FCSTD DOCUMENT  (FreeCAD 0.16R)
Label: chainguard30t
License: All rights reserved
LicenseURL: http://en.wikipedia.org/wiki/All_rights_reserved
objects: Sketcher::SketchObject×12, PartDesign::Pocket×6, PartDesign::Pad×5, Mesh::Feature×4, PartDesign::Fillet×1
note: 35 computed .brp shape members not serialized (recipe doc carries the construction recipe); baked Part::Feature solids carry a one-line shape summary decoded from their .brp

FEATURE [Sketcher::SketchObject] Sketch001
  sketch-geometry (7):
    g0: LineSegment StartX=50 StartY=74 StartZ=0 EndX=0 EndY=74 EndZ=0
    g1: LineSegment StartX=50 StartY=-74 StartZ=0 EndX=0 EndY=-74 EndZ=0
    g2: ArcOfCircle CenterX=0.00010789 CenterY=0 CenterZ=0 NormalX=0 NormalY=0 NormalZ=1 Radius=74 StartAngle=1.5708 EndAngle=4.71239
    g3: Circle CenterX=0 CenterY=0 CenterZ=0 NormalX=0 NormalY=0 NormalZ=1 Radius=45
    g4: LineSegment StartX=73 StartY=51 StartZ=0 EndX=73 EndY=-51 EndZ=0
    g5: ArcOfCircle CenterX=50 CenterY=51 CenterZ=0 NormalX=0 NormalY=0 NormalZ=1 Radius=23 StartAngle=0 EndAngle=1.5708
    g6: ArcOfCircle CenterX=50 CenterY=-51 CenterZ=0 NormalX=0 NormalY=0 NormalZ=1 Radius=23 StartAngle=4.71239 EndAngle=6.28319
  constraints (22):
    c: Horizontal(g0)
    c: Horizontal(g1)
    c: Coincident(g2,g1)
    c: Coincident(g0,g2)
    c: DistanceX(g1,g0) = 0
    c: Equal(g0,g1)
    c: DistanceY(g1,g0) = 148
    c: Symmetric(g1,g0,g-1)
    c: Radius(g3) = 45
    c: Coincident(g3,g-1)
    c: DistanceX(g0,g0) = 50
    c: Vertical(g4)
    c: DistanceX(g-1,g4) = 73
    c: Symmetric(g4,g4,g-1)
    c: DistanceY(g4,g4) = 102
    c: Coincident(g5,g4)
    c: Coincident(g5,g0)
    c: Coincident(g6,g4)
    c: Coincident(g6,g1)
    c: Equal(g5,g6)
    c: Radius(g5) = 23
    c: Radius(g2) = 74
FEATURE [PartDesign::Pad] Pad  label="Faceplate"
  Length = 1.12
  Length2 = 100
  Reversed = true
  Sketch = -> Sketch001
  Type = 0
FEATURE [Sketcher::SketchObject] Sketch002
  sketch-geometry (8):
    g0: LineSegment StartX=50 StartY=74 StartZ=0 EndX=0 EndY=74 EndZ=0
    g1: LineSegment StartX=50 StartY=-74 StartZ=0 EndX=0 EndY=-74 EndZ=0
    g2: ArcOfCircle CenterX=0.000113412 CenterY=0 CenterZ=0 NormalX=0 NormalY=0 NormalZ=1 Radius=74 StartAngle=1.5708 EndAngle=4.71239
    g3: LineSegment StartX=0 StartY=72 StartZ=0 EndX=50 EndY=72 EndZ=0
    g4: LineSegment StartX=0 StartY=-72 StartZ=0 EndX=50 EndY=-72 EndZ=0
    g5: LineSegment StartX=50 StartY=74 StartZ=0 EndX=50 EndY=72 EndZ=0
    g6: LineSegment StartX=50 StartY=-72 StartZ=0 EndX=50 EndY=-74 EndZ=0
    g7: ArcOfCircle CenterX=7.04967e-05 CenterY=0 CenterZ=0 NormalX=0 NormalY=0 NormalZ=1 Radius=72 StartAngle=1.5708 EndAngle=4.71239
  constraints (25):
    c: Horizontal(g0)
    c: Horizontal(g1)
    c: Coincident(g2,g1)
    c: Coincident(g0,g2)
    c: DistanceX(g1,g0) = 0
    c: Equal(g0,g1)
    c: DistanceY(g1,g0) = 148
    c: Symmetric(g1,g0,g-1)
    c: Parallel(g0,g3)
    c: DistanceY(g3,g0) = 2
    c: DistanceY(g1,g4) = 2
    c: Parallel(g4,g1)
    c: DistanceX(g0,g3) = 0
    c: DistanceX(g4) = 0
    c: DistanceX(g0) = 50
    c: Equal(g3,g0)
    c: Equal(g4,g0)
    c: Coincident(g4,g6)
    c: Coincident(g6,g1)
    c: Coincident(g5,g3)
    c: Coincident(g5,g0)
    c: Coincident(g7,g3)
    c: Coincident(g7,g4)
    c: Radius(g7) = 72
    c: Radius(g2) = 74
FEATURE [PartDesign::Pad] Pad001  label="Connector"
  Length = 10
  Length2 = 100
  Sketch = -> Sketch002
  Type = 0
FEATURE [Sketcher::SketchObject] Sketch011
  Placement = pos=(0,74,0) rot=(0,0.707107,0.707107;3.14159rad)
  Support = -> Pad001 [Face1]
  sketch-geometry (4):
    g0: LineSegment StartX=-42 StartY=11 StartZ=0 EndX=-54.6477 EndY=14.0061 EndZ=0
    g1: LineSegment StartX=-54.6477 StartY=14.0061 StartZ=0 EndX=-50.9272 EndY=1.54985 EndZ=0
    g2: LineSegment StartX=-50.9272 StartY=1.54985 StartZ=0 EndX=-42 EndY=11 EndZ=0
    g3: Circle [constr] CenterX=-49.1916 CenterY=8.85198 CenterZ=0 NormalX=0 NormalY=0 NormalZ=1 Radius=7.50555
  constraints (14):
    c: Coincident(g0,g1)
    c: Coincident(g1,g2)
    c: Coincident(g2,g0)
    c: Equal(g0,g1)
    c: Equal(g0,g2)
    c: PointOnObject(g0,g3)
    c: PointOnObject(g1,g3)
    c: PointOnObject(g2,g3)
    c: DistanceY(g-1,g0) = 11
    c: DistanceX(g0,g-1) = 42
    c: Equal(g2,g0)
    c: Equal(g0,g1)
    c: Distance(g2) = 13
    c: Angle(g0) = 2.90824
FEATURE [PartDesign::Pocket] Pocket005  label="Bevel_connector"
  Length = 5
  Sketch = -> Sketch011
  Type = 1
FEATURE [Sketcher::SketchObject] Sketch017
  sketch-geometry (5):
    g0: LineSegment [constr] StartX=-4 StartY=2 StartZ=0 EndX=-27.8283 EndY=-75.9388 EndZ=0
    g1: LineSegment StartX=-43.448 StartY=-67.1734 StartZ=0 EndX=-9.97737 EndY=-77.4064 EndZ=0
    g2: LineSegment StartX=-9.97737 StartY=-77.4064 StartZ=0 EndX=-8.22314 EndY=-71.6686 EndZ=0
    g3: LineSegment StartX=-8.22314 StartY=-71.6686 StartZ=0 EndX=-41.6938 EndY=-61.4356 EndZ=0
    g4: LineSegment StartX=-41.6938 StartY=-61.4356 StartZ=0 EndX=-43.448 EndY=-67.1734 EndZ=0
  constraints (15):
    c: DistanceY(g-1,g0) = 2
    c: DistanceX(g-1,g0) = -4
    c: Angle(g0) = -1.8675
    c: Coincident(g1,g2)
    c: Coincident(g2,g3)
    c: Coincident(g3,g4)
    c: Coincident(g1,g4)
    c: Parallel(g2,g4)
    c: Parallel(g1,g3)
    c: Perpendicular(g2,g1)
    c: Distance(g4) = 6
    c: Distance(g1) = 35
    c: Symmetric(g3,g2,g0)
    c: Distance(g-1,g1) = 80
    c: Distance(g0) = 81.5
FEATURE [Sketcher::SketchObject] Sketch020
  sketch-geometry (4):
    g0: LineSegment StartX=67 StartY=25 StartZ=0 EndX=73 EndY=25 EndZ=0
    g1: LineSegment StartX=73 StartY=25 StartZ=0 EndX=73 EndY=-35 EndZ=0
    g2: LineSegment StartX=73 StartY=-35 StartZ=0 EndX=67 EndY=-35 EndZ=0
    g3: LineSegment StartX=67 StartY=-35 StartZ=0 EndX=67 EndY=25 EndZ=0
  constraints (12):
    c: Coincident(g0,g1)
    c: Coincident(g1,g2)
    c: Coincident(g2,g3)
    c: Coincident(g3,g0)
    c: Horizontal(g0)
    c: Horizontal(g2)
    c: Vertical(g1)
    c: Vertical(g3)
    c: DistanceX(g-1,g0) = 73
    c: DistanceX(g0,g0) = 6
    c: DistanceY(g-1,g0) = 25
    c: DistanceY(g1,g1) = 60
FEATURE [PartDesign::Pad] Pad004  label="SyncBoss"
  Length = 31
  Length2 = 100
  Sketch = -> Sketch020
  Type = 0
FEATURE [Sketcher::SketchObject] Sketch021
  ExternalGeometry = -> [Pad004]
  Placement = pos=(73,0,0) rot=(0.57735,0.57735,0.57735;2.0944rad)
  Support = -> Pad004 [Face2]
  sketch-geometry (1):
    g0: Circle CenterX=-5 CenterY=31 CenterZ=0 NormalX=0 NormalY=0 NormalZ=1 Radius=11.2
  constraints (2):
    c: Symmetric(g-4,g-3,g0)
    c: Radius(g0) = 11.2
FEATURE [PartDesign::Pocket] Pocket  label="SyncHole"
  Length = 5
  Sketch = -> Sketch021
  Type = 1
FEATURE [PartDesign::Pad] Pad005  label="STBoss"
  Length = 31
  Length2 = 1
  Sketch = -> Sketch017
  Type = 4
FEATURE [Sketcher::SketchObject] Sketch022
  ExternalGeometry = -> [Pad005]
  Placement = pos=(-22.4954,-73.5793,0) rot=(0.978386,-0.146221,-0.146221;1.59265rad)
  Support = -> Pad005 [Face1]
  sketch-geometry (1):
    g0: Circle CenterX=-4.40996 CenterY=31 CenterZ=0 NormalX=0 NormalY=0 NormalZ=1 Radius=11.2
  constraints (2):
    c: Symmetric(g-4,g-3,g0)
    c: Radius(g0) = 11.2
FEATURE [PartDesign::Pocket] Pocket006  label="SThole"
  Length = 5
  Sketch = -> Sketch022
  Type = 1
FEATURE [Sketcher::SketchObject] Sketch024
  sketch-geometry (6):
    g0: ArcOfCircle CenterX=0 CenterY=0 CenterZ=0 NormalX=0 NormalY=0 NormalZ=1 Radius=48 StartAngle=1.34179 EndAngle=4.9414
    g1: Circle CenterX=0 CenterY=0 CenterZ=0 NormalX=0 NormalY=0 NormalZ=1 Radius=45
    g2: LineSegment StartX=10.8966 StartY=46.7468 StartZ=0 EndX=65 EndY=35.4994 EndZ=0
    g3: LineSegment StartX=65 StartY=35.5006 StartZ=0 EndX=65 EndY=-35.4994 EndZ=0
    g4: LineSegment StartX=65 StartY=-35.4994 StartZ=0 EndX=10.8966 EndY=-46.7468 EndZ=0
    g5: LineSegment StartX=65 StartY=35.5 StartZ=0 EndX=65 EndY=-35.5 EndZ=0
  constraints (14):
    c: Coincident(g0,g-1)
    c: Radius(g0) = 48
    c: Coincident(g1,g-1)
    c: Radius(g1) = 45
    c: Coincident(g3,g4)
    c: Coincident(g0,g2)
    c: Distance(g3) = 71
    c: DistanceX(g-1,g2) = 65
    c: Equal(g4,g2)
    c: Vertical(g3)
    c: Symmetric(g2,g3,g-1)
    c: Distance(g2) = 55.2601
    c: DistanceY(g-1,g0) = 46.7468
    c: DistanceX(g0) = 10.8966
FEATURE [Sketcher::SketchObject] Sketch028
  ExternalGeometry = -> [Pocket]
  Placement = pos=(0,0,31) rot=(0,0,1;0rad)
  Support = -> Pocket [Face5]
  sketch-geometry (2):
    g0: Circle CenterX=70 CenterY=9 CenterZ=0 NormalX=0 NormalY=0 NormalZ=1 Radius=0.8
    g1: Circle CenterX=70 CenterY=-19 CenterZ=0 NormalX=0 NormalY=0 NormalZ=1 Radius=0.8
  constraints (6):
    c: DistanceY(g-4,g0) = 2.8
    c: DistanceX(g0,g-4) = 3
    c: DistanceX(g1,g-6) = 3
    c: DistanceY(g1,g-5) = 2.8
    c: Equal(g1,g0)
    c: Radius(g1) = 0.8
FEATURE [PartDesign::Pocket] Pocket010  label="SyncScrewHoles"
  Length = 15
  Sketch = -> Sketch028
  Type = 0
FEATURE [Sketcher::SketchObject] Sketch029
  ExternalGeometry = -> [Pocket010]
  Placement = pos=(73,0,0) rot=(0.57735,0.57735,0.57735;2.0944rad)
  Support = -> Pocket010 [Face3]
  sketch-geometry (6):
    g0: LineSegment StartX=25 StartY=3 StartZ=0 EndX=12.5 EndY=32 EndZ=0
    g1: LineSegment StartX=12.5 StartY=32 StartZ=0 EndX=-22.5 EndY=32 EndZ=0
    g2: LineSegment StartX=-22.5 StartY=32 StartZ=0 EndX=-35 EndY=3 EndZ=0
    g3: LineSegment StartX=-35 StartY=3 StartZ=0 EndX=-38.2949 EndY=52.1665 EndZ=0
    g4: LineSegment StartX=-38.2949 StartY=52.1665 StartZ=0 EndX=33.0613 EndY=52.1665 EndZ=0
    g5: LineSegment StartX=33.0613 StartY=52.1665 StartZ=0 EndX=25 EndY=3 EndZ=0
  constraints (18):
    c: Coincident(g0,g1)
    c: Horizontal(g1)
    c: Coincident(g1,g2)
    c: Coincident(g2,g3)
    c: Coincident(g3,g4)
    c: Horizontal(g4)
    c: Coincident(g4,g5)
    c: Coincident(g0,g5)
    c: DistanceX(g-4,g0) = 6.3
    c: DistanceX(g1,g-4) = 6.3
    c: DistanceX(g-3,g0) = 0
    c: DistanceX(g2,g-6) = 0
    c: DistanceX(g4,g4) = 71.3562
    c: Distance(g3) = 49.2768
    c: Distance(g5) = 49.823
    c: DistanceY(g-4,g1) = 1
    c: DistanceY(g-6,g2) = 3
    c: DistanceY(g-3,g0) = 3
FEATURE [PartDesign::Pocket] Pocket011  label="SyncBigBevel"
  Length = 5
  Sketch = -> Sketch029
  Type = 1
FEATURE [Sketcher::SketchObject] Sketch
  ExternalGeometry = -> [Pad]
  Support = -> Pad [Face8]
  sketch-geometry (5):
    g0: Circle CenterX=0 CenterY=0 CenterZ=0 NormalX=0 NormalY=0 NormalZ=1 Radius=45
    g1: ArcOfCircle CenterX=0 CenterY=0 CenterZ=0 NormalX=0 NormalY=0 NormalZ=1 Radius=54 StartAngle=1.47009 EndAngle=4.8131
    g2: LineSegment StartX=5.42905 StartY=53.7264 StartZ=0 EndX=73 EndY=50 EndZ=0
    g3: LineSegment StartX=73 StartY=50 StartZ=0 EndX=73 EndY=-50 EndZ=0
    g4: LineSegment StartX=73 StartY=-50 StartZ=0 EndX=5.42905 EndY=-53.7264 EndZ=0
  constraints (14):
    c: Coincident(g2,g3)
    c: Vertical(g3)
    c: Coincident(g3,g4)
    c: Coincident(g0,g-1)
    c: Coincident(g1,g-1)
    c: Radius(g0) = 45
    c: Radius(g1) = 54
    c: DistanceX(g-3,g2) = 0
    c: DistanceY(g3,g-1) = 50
    c: DistanceY(g-1,g2) = 50
    c: Coincident(g1,g2)
    c: Coincident(g1,g4)
    c: Symmetric(g1,g1,g-1)
    c: DistanceX(g-1,g1) = 5.42905
FEATURE [PartDesign::Pad] Pad008  label="FaceStiffener"
  Length = 1
  Length2 = 100
  Sketch = -> Sketch
  Type = 0
FEATURE [PartDesign::Fillet] Fillet  label="SyncFillets"
  Base = -> Pocket011 [Edge13,Edge14,Edge15,Edge3,Edge9,Edge21,Edge19,Edge22]
  Radius = 1
FEATURE [Sketcher::SketchObject] Sketch030
  ExternalGeometry = -> [Pocket006]
  Placement = pos=(0,0,31) rot=(0,0,1;0rad)
  Support = -> Pocket006 [Face4]
  sketch-geometry (2):
    g0: Circle CenterX=-12.6107 CenterY=-73.4436 CenterZ=0 NormalX=0 NormalY=0 NormalZ=1 Radius=0.8
    g1: Circle CenterX=-39.049 CenterY=-65.3606 CenterZ=0 NormalX=0 NormalY=0 NormalZ=1 Radius=0.8
  constraints (6):
    c: Equal(g1,g0)
    c: Radius(g1) = 0.8
    c: Distance(g0,g-4) = 25.2
    c: Distance(g-3,g1) = 25.2
    c: Distance(g-5,g1) = 4
    c: Distance(g-6,g0) = 4
FEATURE [PartDesign::Pocket] Pocket012  label="STScrewHoles"
  Length = 12
  Sketch = -> Sketch030
  Type = 0
FEATURE [Mesh::Feature] Mesh  label="Bevel_connector (Meshed)"
FEATURE [Mesh::Feature] Mesh001  label="FaceStiffener (Meshed)"
FEATURE [Mesh::Feature] Mesh002  label="SyncFillets (Meshed)"
FEATURE [Mesh::Feature] Mesh003  label="STScrewHoles (Meshed)"
